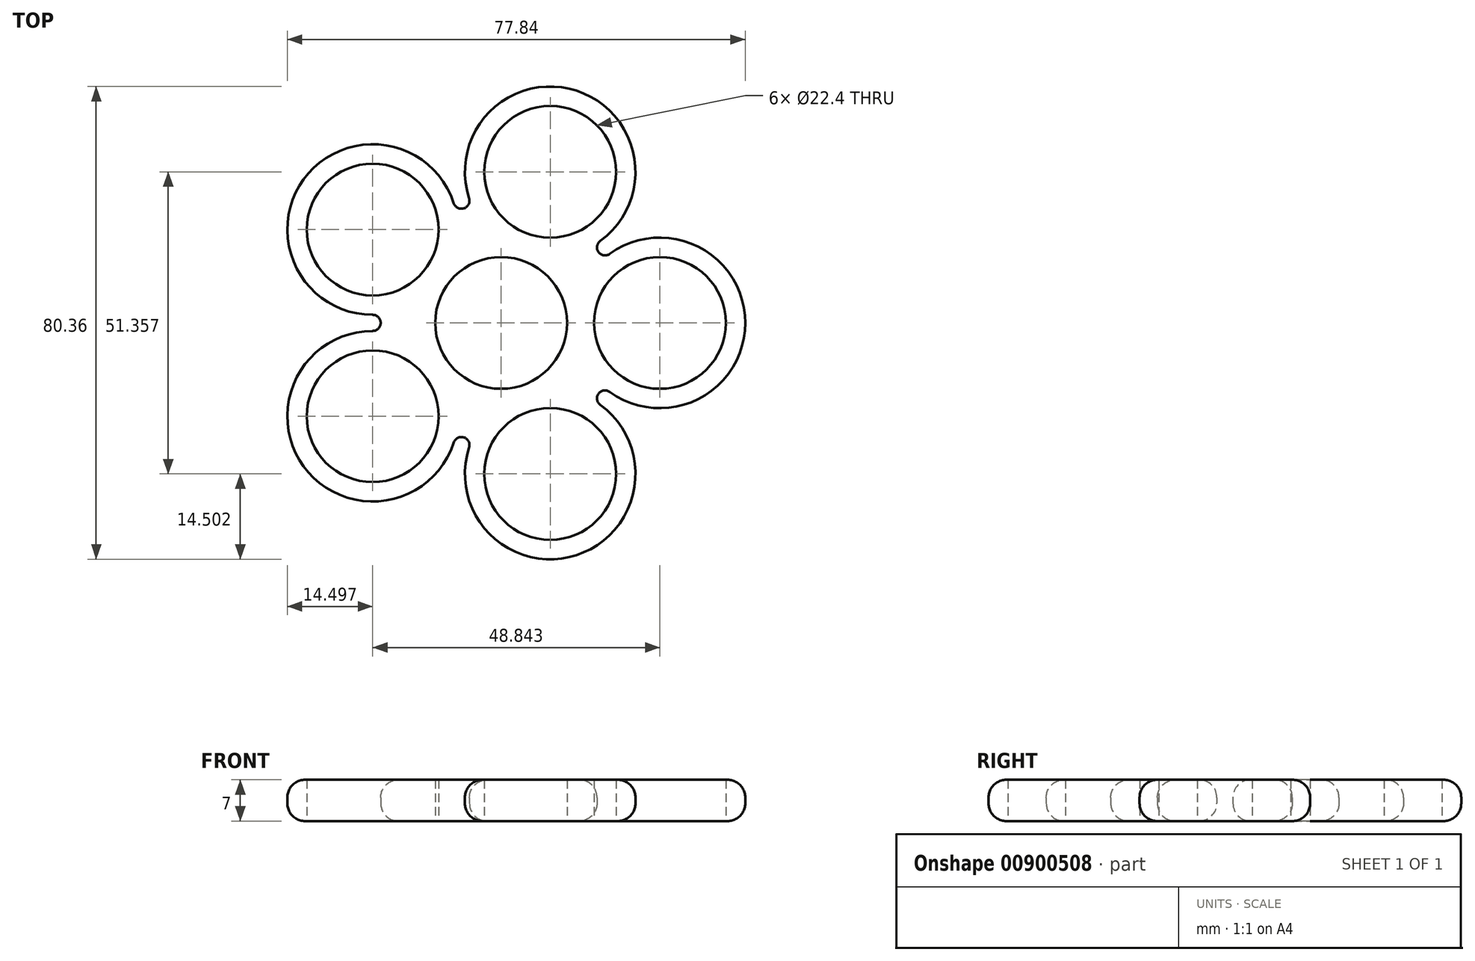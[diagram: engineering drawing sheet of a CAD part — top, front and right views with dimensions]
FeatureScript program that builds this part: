
annotation { "Feature Type Name" : "Feature", "Feature Type Description" : "" }
export const myFeature = defineFeature(function(context is Context, id is Id, definition is map)
    precondition{}
    {
        {
            assignVariable(context, id + "F0", {"name" : "w", "anyValue" : 7});
        }
        {
            var Q0;
            Q0=qCreatedBy(makeId("Top.planeOp"),FACE);
            var sketch = newSketch(context, id + "F1", { "sketchPlane" : qUnion([Q0])});
            skCircle(sketch, "E0", {"center": v(0, 0) * mm, "radius": 11.2 * mm});
            skCircle(sketch, "E1.cCircle", {"center": v(0, 0) * mm, "radius": 27 * mm, "construction": true});
            skLineSegment(sketch, "E1.0", {"start": v(27, 0) * mm, "end": v(8.34, -25.68) * mm, "construction": true});
            skLineSegment(sketch, "E1.1", {"start": v(8.34, -25.68) * mm, "end": v(-21.84, -15.87) * mm, "construction": true});
            skLineSegment(sketch, "E1.2", {"start": v(-21.84, -15.87) * mm, "end": v(-21.84, 15.87) * mm, "construction": true});
            skLineSegment(sketch, "E1.3", {"start": v(-21.84, 15.87) * mm, "end": v(8.34, 25.68) * mm, "construction": true});
            skLineSegment(sketch, "E1.4", {"start": v(8.34, 25.68) * mm, "end": v(27, 0) * mm, "construction": true});
            skCircle(sketch, "E2", {"center": v(27, 0) * mm, "radius": 14.5 * mm});
            skCircle(sketch, "E3", {"center": v(8.34, 25.68) * mm, "radius": 14.5 * mm});
            skCircle(sketch, "E4", {"center": v(-21.84, 15.87) * mm, "radius": 14.5 * mm});
            skCircle(sketch, "E5", {"center": v(-21.84, -15.87) * mm, "radius": 14.5 * mm});
            skCircle(sketch, "E6", {"center": v(8.34, -25.68) * mm, "radius": 14.5 * mm});
            skLineSegment(sketch, "E7", {"start": v(16.87, 13.95) * mm, "end": v(39.22, 30.2) * mm, "construction": true});
            skArc(sketch, "E8", {"start": v(16.87, 13.95) * mm, "mid": v(16.56, 12.03) * mm, "end": v(18.48, 11.73) * mm});
            skLineSegment(sketch, "E9", {"start": v(-8.05, 20.35) * mm, "end": v(-19.48, 55.5) * mm, "construction": true});
            skLineSegment(sketch, "E10", {"start": v(-21.84, -1.37) * mm, "end": v(-57.39, -1.37) * mm, "construction": true});
            skLineSegment(sketch, "E11", {"start": v(-5.45, -21.2) * mm, "end": v(-13.51, -46.02) * mm, "construction": true});
            skLineSegment(sketch, "E12", {"start": v(16.87, -13.95) * mm, "end": v(48.13, -36.66) * mm, "construction": true});
            skArc(sketch, "E13", {"start": v(-8.05, 20.35) * mm, "mid": v(-6.33, 19.47) * mm, "end": v(-5.45, 21.2) * mm});
            skArc(sketch, "E14", {"start": v(-21.84, -1.37) * mm, "mid": v(-20.47, 0) * mm, "end": v(-21.84, 1.37) * mm});
            skArc(sketch, "E15", {"start": v(16.87, -13.95) * mm, "mid": v(16.56, -12.03) * mm, "end": v(18.48, -11.73) * mm});
            skArc(sketch, "E16", {"start": v(-5.45, -21.2) * mm, "mid": v(-6.33, -19.47) * mm, "end": v(-8.05, -20.35) * mm});
            skCircle(sketch, "E17", {"center": v(27, 0) * mm, "radius": 11.2 * mm});
            skCircle(sketch, "E18", {"center": v(8.34, 25.68) * mm, "radius": 11.2 * mm});
            skCircle(sketch, "E19", {"center": v(-21.84, 15.87) * mm, "radius": 11.2 * mm});
            skCircle(sketch, "E20", {"center": v(-21.84, -15.87) * mm, "radius": 11.2 * mm});
            skCircle(sketch, "E21", {"center": v(8.34, -25.68) * mm, "radius": 11.2 * mm});
            skSolve(sketch);
        }
        {
            var Q0;
            Q0 = qSketchRegion(id + "F1", true);
            extrude(context, id + "F2", {"entities" : qUnion([Q0]), "endBound" : BoundingType.SYMMETRIC, "depth" : (getVariable(context, 'w')) * mm, "offsetDistance" : 25 * mm});
        }
        {
            var Q0;
            Q0=makeQuery(id+"F2.opExtrude","CAP_EDGE",EDGE,{"disambiguationData":[OSD([sQuery(id+"F1.wireOp",EDGE,"E5")])],"isStart":false});
            var Q1;
            Q1=makeQuery(id+"F2.opExtrude","CAP_EDGE",EDGE,{"disambiguationData":[OSD([sQuery(id+"F1.wireOp",EDGE,"E5")])],"isStart":true});
            fillet(context, id + "F3", {"entities" : qUnion([Q0, Q1]), "radius" : (getVariable(context, 'w') / 2 - 0.5) * mm, "tangentPropagation" : true, "allowEdgeOverflow" : false});
        }
    });
